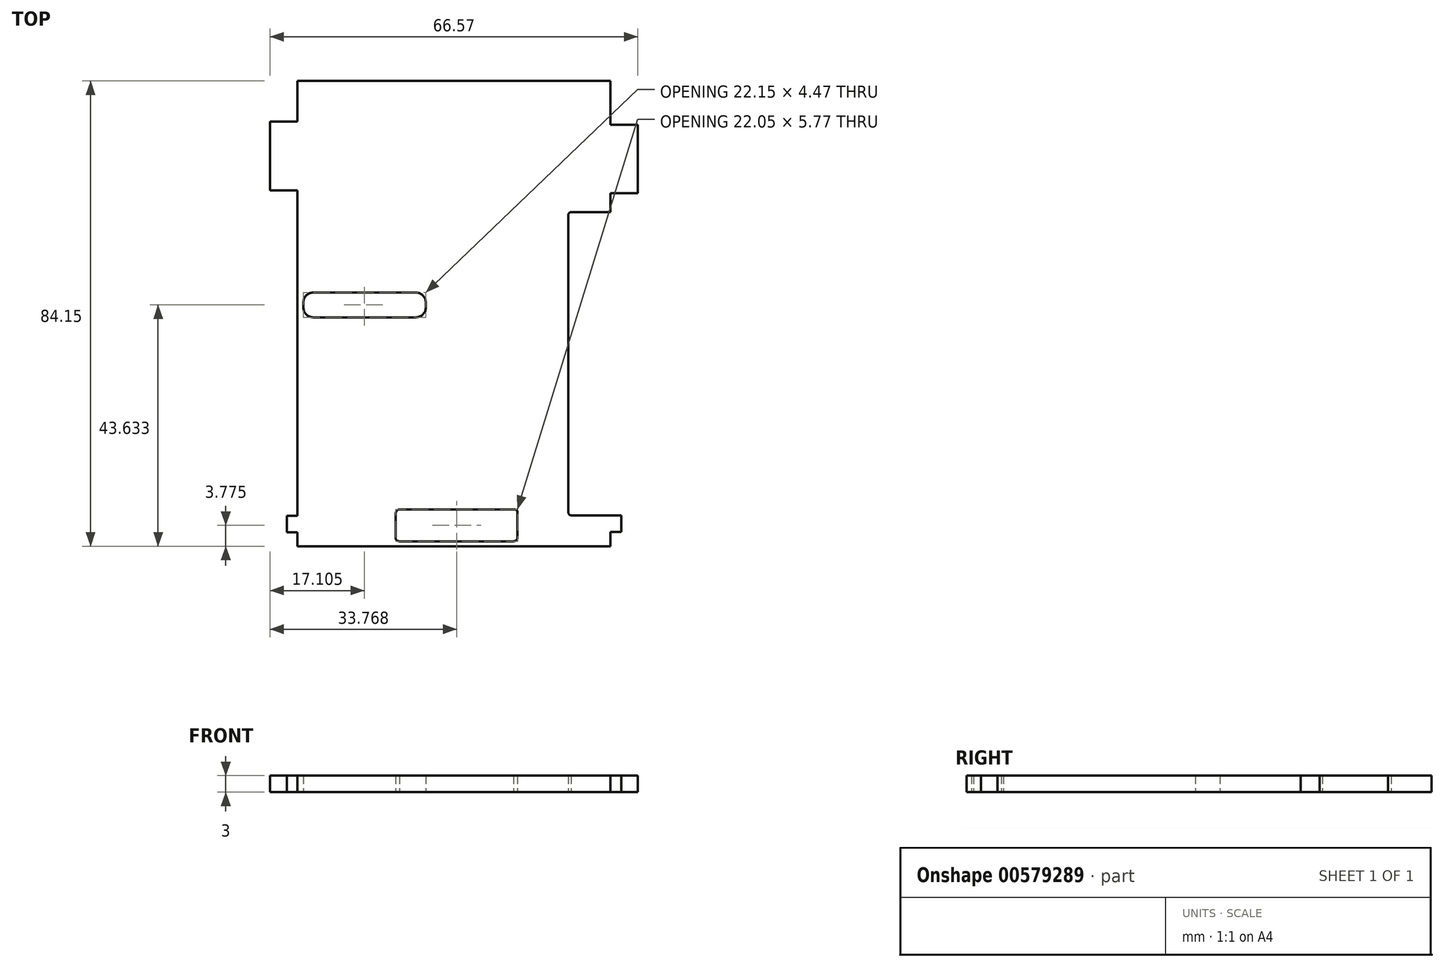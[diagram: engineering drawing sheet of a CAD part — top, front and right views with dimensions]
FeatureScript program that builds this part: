
annotation { "Feature Type Name" : "Feature", "Feature Type Description" : "" }
export const myFeature = defineFeature(function(context is Context, id is Id, definition is map)
    precondition{}
    {
        {
            var Q0;
            Q0=qCreatedBy(makeId("Top.planeOp"),FACE);
            var sketch = newSketch(context, id + "F0", { "sketchPlane" : qUnion([Q0])});
            skLineSegment(sketch, "E0.bottom", {"start": v(-14.05, 28.33) * mm, "end": v(42.6, 28.33) * mm});
            skLineSegment(sketch, "E0.left", {"start": v(-14.05, 28.33) * mm, "end": v(-14.05, 20.98) * mm});
            skLineSegment(sketch, "E0.right", {"start": v(42.6, 28.33) * mm, "end": v(42.6, 20.45) * mm});
            skLineSegment(sketch, "E1.bottom", {"start": v(42.6, 20.45) * mm, "end": v(47.56, 20.45) * mm});
            skLineSegment(sketch, "E1.top", {"start": v(42.6, 8.03) * mm, "end": v(47.56, 8.03) * mm});
            skLineSegment(sketch, "E1.right", {"start": v(47.56, 20.45) * mm, "end": v(47.56, 8.03) * mm});
            skLineSegment(sketch, "E2.bottom", {"start": v(42.6, -50.23) * mm, "end": v(44.53, -50.23) * mm});
            skLineSegment(sketch, "E2.top", {"start": v(42.6, -53.23) * mm, "end": v(44.56, -53.23) * mm});
            skLineSegment(sketch, "E2.right", {"start": v(44.53, -50.23) * mm, "end": v(44.56, -53.23) * mm});
            skLineSegment(sketch, "E3.trimOffspring", {"start": v(42.6, 8.03) * mm, "end": v(42.6, 4.62) * mm});
            skLineSegment(sketch, "E4.trimOffspring", {"start": v(42.6, -53.23) * mm, "end": v(42.6, -55.82) * mm});
            skLineSegment(sketch, "E5.MirrorCS", {"start": v(-14.05, -50.3) * mm, "end": v(-15.98, -50.3) * mm});
            skLineSegment(sketch, "E6.MirrorCS", {"start": v(-14.05, -53.3) * mm, "end": v(-15.98, -53.3) * mm});
            skLineSegment(sketch, "E7.MirrorCS", {"start": v(-15.98, -50.3) * mm, "end": v(-15.98, -53.3) * mm});
            skLineSegment(sketch, "E8.MirrorCS", {"start": v(-19, 20.98) * mm, "end": v(-19, 8.56) * mm});
            skLineSegment(sketch, "E9.MirrorCS", {"start": v(-14.05, 8.56) * mm, "end": v(-19, 8.56) * mm});
            skLineSegment(sketch, "E10.MirrorCS", {"start": v(-14.05, 20.98) * mm, "end": v(-19, 20.98) * mm});
            skPoint(sketch, "E11.end.orphan", {"position": v(14.28, 28.33) * mm});
            skPoint(sketch, "E11.start.orphan", {"position": v(14.28, -56.88) * mm});
            skLineSegment(sketch, "E12.trimOffspring", {"start": v(-14.05, 8.56) * mm, "end": v(-14.05, -50.3) * mm});
            skLineSegment(sketch, "E13.trimOffspring", {"start": v(-14.05, -53.3) * mm, "end": v(-14.05, -55.82) * mm});
            skLineSegment(sketch, "E14.bottom", {"start": v(42.6, 4.62) * mm, "end": v(35.47, 4.62) * mm});
            skLineSegment(sketch, "E14.top", {"start": v(40, -50.23) * mm, "end": v(35.47, -50.23) * mm});
            skLineSegment(sketch, "E14.right", {"start": v(34.97, 4.12) * mm, "end": v(34.97, -49.73) * mm});
            skLineSegment(sketch, "E15.bottom", {"start": v(14.76, -49.16) * mm, "end": v(25.08, -49.16) * mm});
            skLineSegment(sketch, "E15.top", {"start": v(14.76, -54.93) * mm, "end": v(25.08, -54.93) * mm});
            skLineSegment(sketch, "E16", {"start": v(25.78, -54.23) * mm, "end": v(25.78, -49.56) * mm});
            skArc(sketch, "E17", {"start": v(25.78, -49.56) * mm, "mid": v(25.5, -49.25) * mm, "end": v(25.08, -49.16) * mm});
            skArc(sketch, "E18", {"start": v(25.08, -54.93) * mm, "mid": v(25.58, -54.72) * mm, "end": v(25.78, -54.23) * mm});
            skLineSegment(sketch, "E19.MirrorCS", {"start": v(3.73, -54.53) * mm, "end": v(3.73, -49.86) * mm});
            skLineSegment(sketch, "E20.MirrorCS", {"start": v(14.76, -54.93) * mm, "end": v(4.43, -54.93) * mm});
            skArc(sketch, "E21.MirrorCS", {"start": v(3.73, -49.86) * mm, "mid": v(3.94, -49.37) * mm, "end": v(4.43, -49.16) * mm});
            skLineSegment(sketch, "E22.MirrorCS", {"start": v(14.76, -49.16) * mm, "end": v(4.43, -49.16) * mm});
            skArc(sketch, "E23.MirrorCS", {"start": v(4.43, -54.93) * mm, "mid": v(4.02, -54.84) * mm, "end": v(3.73, -54.53) * mm});
            skLineSegment(sketch, "E24.bottom", {"start": v(-11.2, -9.95) * mm, "end": v(7.4, -9.95) * mm});
            skLineSegment(sketch, "E24.top", {"start": v(-11.2, -14.42) * mm, "end": v(7.4, -14.42) * mm});
            skLineSegment(sketch, "E24.left", {"start": v(-12.98, -11.73) * mm, "end": v(-12.98, -12.64) * mm});
            skLineSegment(sketch, "E24.right", {"start": v(9.17, -11.73) * mm, "end": v(9.17, -12.64) * mm});
            skArc(sketch, "E25", {"start": v(35.47, 4.62) * mm, "mid": v(35.11, 4.48) * mm, "end": v(34.97, 4.12) * mm});
            skPoint(sketch, "E26.start.orphan", {"position": v(34.97, 4.62) * mm});
            skArc(sketch, "E27", {"start": v(34.97, -49.73) * mm, "mid": v(35.11, -50.08) * mm, "end": v(35.47, -50.23) * mm});
            skPoint(sketch, "E28.start.orphan", {"position": v(34.97, -50.23) * mm});
            skArc(sketch, "E29", {"start": v(-11.2, -9.95) * mm, "mid": v(-12.46, -10.47) * mm, "end": v(-12.98, -11.73) * mm});
            skArc(sketch, "E30", {"start": v(-12.98, -12.64) * mm, "mid": v(-12.46, -13.9) * mm, "end": v(-11.2, -14.42) * mm});
            skArc(sketch, "E31", {"start": v(9.17, -11.73) * mm, "mid": v(8.65, -10.47) * mm, "end": v(7.4, -9.95) * mm});
            skArc(sketch, "E32", {"start": v(7.4, -14.42) * mm, "mid": v(8.65, -13.9) * mm, "end": v(9.17, -12.64) * mm});
            skPoint(sketch, "E33.orphan", {"position": v(-12.98, -9.95) * mm});
            skPoint(sketch, "E34.start.orphan", {"position": v(-12.98, -14.42) * mm});
            skPoint(sketch, "E35.start.orphan", {"position": v(9.17, -14.42) * mm});
            skPoint(sketch, "E36.start.orphan", {"position": v(9.17, -9.95) * mm});
            skLineSegment(sketch, "E37.bottom", {"start": v(-14.05, -55.82) * mm, "end": v(42.6, -55.82) * mm});
            skPoint(sketch, "E38.orphan", {"position": v(42.6, -56.88) * mm});
            skPoint(sketch, "E39.orphan", {"position": v(-14.05, -56.88) * mm});
            skLineSegment(sketch, "E40", {"start": v(42.6, -50.23) * mm, "end": v(40, -50.23) * mm});
            skSolve(sketch);
        }
        {
            var Q0;
            Q0=makeQuery(id+"F0.imprint","IMPRINT",FACE,{"disambiguationData":[TD([[makeQuery(id+"F0.imprint","IMPRINT",EDGE,{"derivedFrom":sQuery(id+"F0.wireOp",EDGE,"E0.bottom")}),-1.0]])]});
            extrude(context, id + "F1", {"entities" : qUnion([Q0]), "depth" : 3 * mm, "offsetDistance" : 25.4 * mm});
        }
    });
